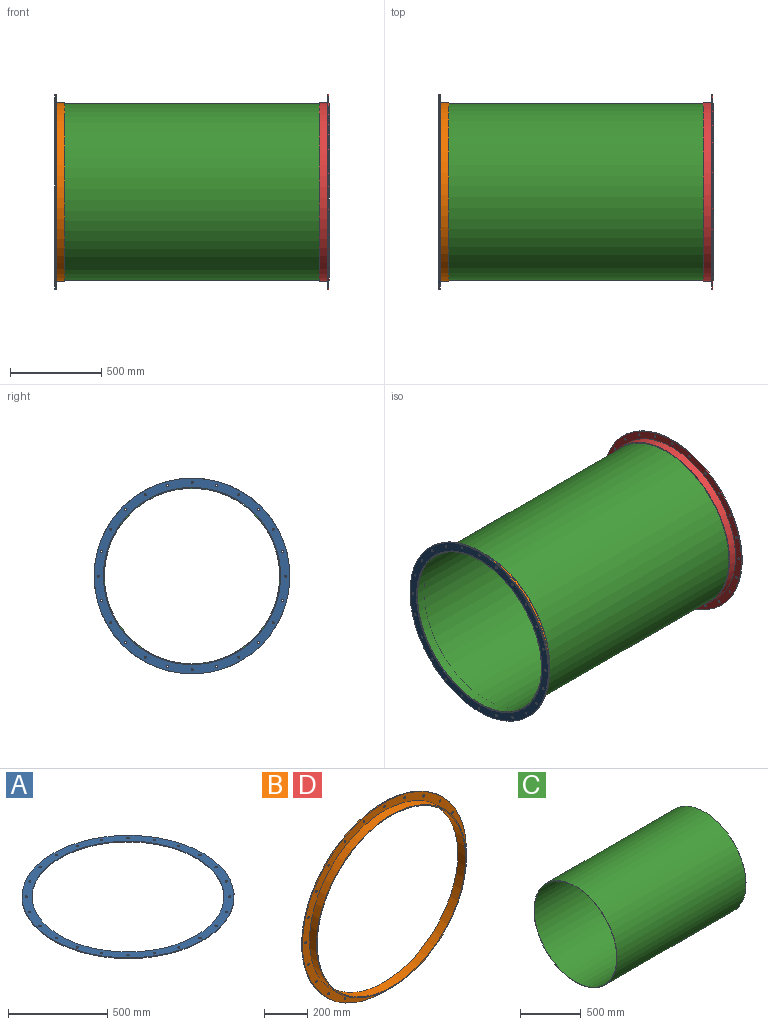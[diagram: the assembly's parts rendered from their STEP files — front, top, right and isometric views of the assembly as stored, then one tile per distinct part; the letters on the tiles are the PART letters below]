
ASSEMBLY  parts=4 mates=3
PART A: 28 faces, bbox 1070.1x1070.1x4.8 mm
  f0: cylinder r=5.56mm len=11.11mm, axis (0,0,-1), area 166.3mm2, adj f26,f27
  f1: cylinder r=5.56mm len=11.11mm, axis (0,0,-1), area 166.3mm2, adj f26,f27
  f2: cylinder r=5.56mm len=11.11mm, axis (0,0,-1), area 166.3mm2, adj f26,f27
  f3: cylinder r=5.56mm len=11.11mm, axis (0,0,-1), area 166.3mm2, adj f26,f27
  f4: cylinder r=5.56mm len=11.11mm, axis (0,0,-1), area 166.3mm2, adj f26,f27
  f5: cylinder r=5.56mm len=11.11mm, axis (0,0,-1), area 166.3mm2, adj f26,f27
  f6: cylinder r=5.56mm len=11.11mm, axis (0,0,-1), area 166.3mm2, adj f26,f27
  f7: cylinder r=5.56mm len=11.11mm, axis (0,0,-1), area 166.3mm2, adj f26,f27
  f8: cylinder r=5.56mm len=11.11mm, axis (0,0,-1), area 166.3mm2, adj f26,f27
  f9: cylinder r=5.56mm len=11.11mm, axis (0,0,-1), area 166.3mm2, adj f26,f27
  f10: cylinder r=5.56mm len=11.11mm, axis (0,0,-1), area 166.3mm2, adj f26,f27
  f11: cylinder r=5.56mm len=11.11mm, axis (0,0,-1), area 166.3mm2, adj f26,f27
  f12: cylinder r=5.56mm len=11.11mm, axis (0,0,-1), area 166.3mm2, adj f26,f27
  f13: cylinder r=5.56mm len=11.11mm, axis (0,0,-1), area 166.3mm2, adj f26,f27
  f14: cylinder r=5.56mm len=11.11mm, axis (0,0,-1), area 166.3mm2, adj f26,f27
  f15: cylinder r=5.56mm len=11.11mm, axis (0,0,-1), area 166.3mm2, adj f26,f27
  f16: cylinder r=5.56mm len=11.11mm, axis (0,0,-1), area 166.3mm2, adj f26,f27
  f17: cylinder r=5.56mm len=11.11mm, axis (0,0,-1), area 166.3mm2, adj f26,f27
  f18: cylinder r=5.56mm len=11.11mm, axis (0,0,-1), area 166.3mm2, adj f26,f27
  f19: cylinder r=5.56mm len=11.11mm, axis (0,0,-1), area 166.3mm2, adj f26,f27
  f20: cylinder r=5.56mm len=11.11mm, axis (0,0,-1), area 166.3mm2, adj f26,f27
  f21: cylinder r=5.56mm len=11.11mm, axis (0,0,-1), area 166.3mm2, adj f26,f27
  f22: cylinder r=5.56mm len=11.11mm, axis (0,0,-1), area 166.3mm2, adj f26,f27
  f23: cylinder r=484.25mm len=968.5mm, axis (0,0,-1), area 14490.6mm2, adj f26,f27
  f24: cylinder r=5.56mm len=11.11mm, axis (0,0,-1), area 166.3mm2, adj f26,f27
  f25: cylinder r=535.05mm len=1070.1mm, axis (0,0,-1), area 16010.7mm2, adj f26,f27
  f26: plane 1070.1x1070.1mm, normal (0,0,1), area 160345.7mm2, adj f0,f1,f2,f3,f4,f5,f6,f7
  f27: plane 1070.1x1070.1mm, normal (0,0,-1), area 160345.7mm2, adj f0,f1,f2,f3,f4,f5,f6,f7
PART B: 30 faces, bbox 1070.1x50.8x1070.1 mm
  f0: cylinder r=5.56mm len=11.11mm, axis (0,1,0), area 166.3mm2, adj f25,f26
  f1: cylinder r=5.56mm len=11.11mm, axis (0,1,0), area 166.3mm2, adj f25,f26
  f2: cylinder r=5.56mm len=11.11mm, axis (0,1,0), area 166.3mm2, adj f25,f26
  f3: cylinder r=5.56mm len=11.11mm, axis (0,1,0), area 166.3mm2, adj f25,f26
  f4: cylinder r=5.56mm len=11.11mm, axis (0,1,0), area 166.3mm2, adj f25,f26
  f5: cylinder r=5.56mm len=11.11mm, axis (0,1,0), area 166.3mm2, adj f25,f26
  f6: cylinder r=5.56mm len=11.11mm, axis (0,1,0), area 166.3mm2, adj f25,f26
  f7: cylinder r=5.56mm len=11.11mm, axis (0,1,0), area 166.3mm2, adj f25,f26
  f8: cylinder r=5.56mm len=11.11mm, axis (0,1,0), area 166.3mm2, adj f25,f26
  f9: cylinder r=5.56mm len=11.11mm, axis (0,1,0), area 166.3mm2, adj f25,f26
  f10: cylinder r=5.56mm len=11.11mm, axis (0,1,0), area 166.3mm2, adj f25,f26
  f11: cylinder r=5.56mm len=11.11mm, axis (0,1,0), area 166.3mm2, adj f25,f26
  f12: cylinder r=5.56mm len=11.11mm, axis (0,1,0), area 166.3mm2, adj f25,f26
  f13: cylinder r=5.56mm len=11.11mm, axis (0,1,0), area 166.3mm2, adj f25,f26
  f14: cylinder r=5.56mm len=11.11mm, axis (0,1,0), area 166.3mm2, adj f25,f26
  f15: cylinder r=5.56mm len=11.11mm, axis (0,1,0), area 166.3mm2, adj f25,f26
  f16: cylinder r=5.56mm len=11.11mm, axis (0,1,0), area 166.3mm2, adj f25,f26
  f17: cylinder r=5.56mm len=11.11mm, axis (0,1,0), area 166.3mm2, adj f25,f26
  f18: cylinder r=5.56mm len=11.11mm, axis (0,1,0), area 166.3mm2, adj f25,f26
  f19: cylinder r=5.56mm len=11.11mm, axis (0,1,0), area 166.3mm2, adj f25,f26
  f20: cylinder r=5.56mm len=11.11mm, axis (0,1,0), area 166.3mm2, adj f25,f26
  f21: cylinder r=5.56mm len=11.11mm, axis (0,1,0), area 166.3mm2, adj f25,f26
  f22: cylinder r=5.56mm len=11.11mm, axis (0,1,0), area 166.3mm2, adj f25,f26
  f23: cylinder r=5.56mm len=11.11mm, axis (0,1,0), area 166.3mm2, adj f25,f26
  f24: cylinder r=535.05mm len=1070.1mm, axis (0,1,0), area 16010.7mm2, adj f25,f26
  f25: plane 1070.1x1070.1mm, normal (0,-1,0), area 145783.9mm2, adj f0,f1,f2,f3,f4,f5,f6,f7
  f26: plane 1070.1x1070.1mm, normal (0,1,0), area 160345.7mm2, adj f0,f1,f2,f3,f4,f5,f6,f7
  f27: cylinder r=484.25mm len=968.5mm, axis (0,1,0), area 154566mm2, adj f26,f29
  f28: cylinder r=489.01mm len=978.03mm, axis (0,1,0), area 141453.1mm2, adj f25,f29
  f29: plane 978.03x978.03mm, normal (0,-1,0), area 14561.8mm2, adj f27,f28
PART C: 4 faces, bbox 1498.6x965.2x965.2 mm
  f0: plane 965.2x965.2mm, normal (1,0,0), area 10322.5mm2, adj f1,f2
  f1: cylinder r=479.18mm len=1498.6mm, axis (-1,0,0), area 4511984.9mm2, adj f0,f3
  f2: cylinder r=482.6mm len=1498.6mm, axis (-1,0,0), area 4544152.7mm2, adj f0,f3
  f3: plane 965.2x965.2mm, normal (-1,0,0), area 10322.5mm2, adj f1,f2
PART D: same geometry as B
PLACE A rot(axis=(0.71,0,0.71),180deg) t=(-383.98,196.63,-23.49)mm
PLACE B rot(axis=(0.58,-0.58,0.58),120deg) t=(-379.22,196.63,-23.49)mm
PLACE C t=(-381.6,196.63,-23.49)mm
PLACE D rot(axis=(0.58,0.58,-0.58),120deg) t=(1113.83,196.63,-23.49)mm
MATE fastened D.f27 <-> C.f2  axis (1,0,0) through (1113.83,196.63,-23.49)mm
MATE fastened A.f23 <-> B.f27  axis (1,0,0) through (-379.22,196.63,-23.49)mm
MATE fastened A.f23 <-> C.f2  axis (-1,0,0) through (-381.6,196.63,-23.49)mm
